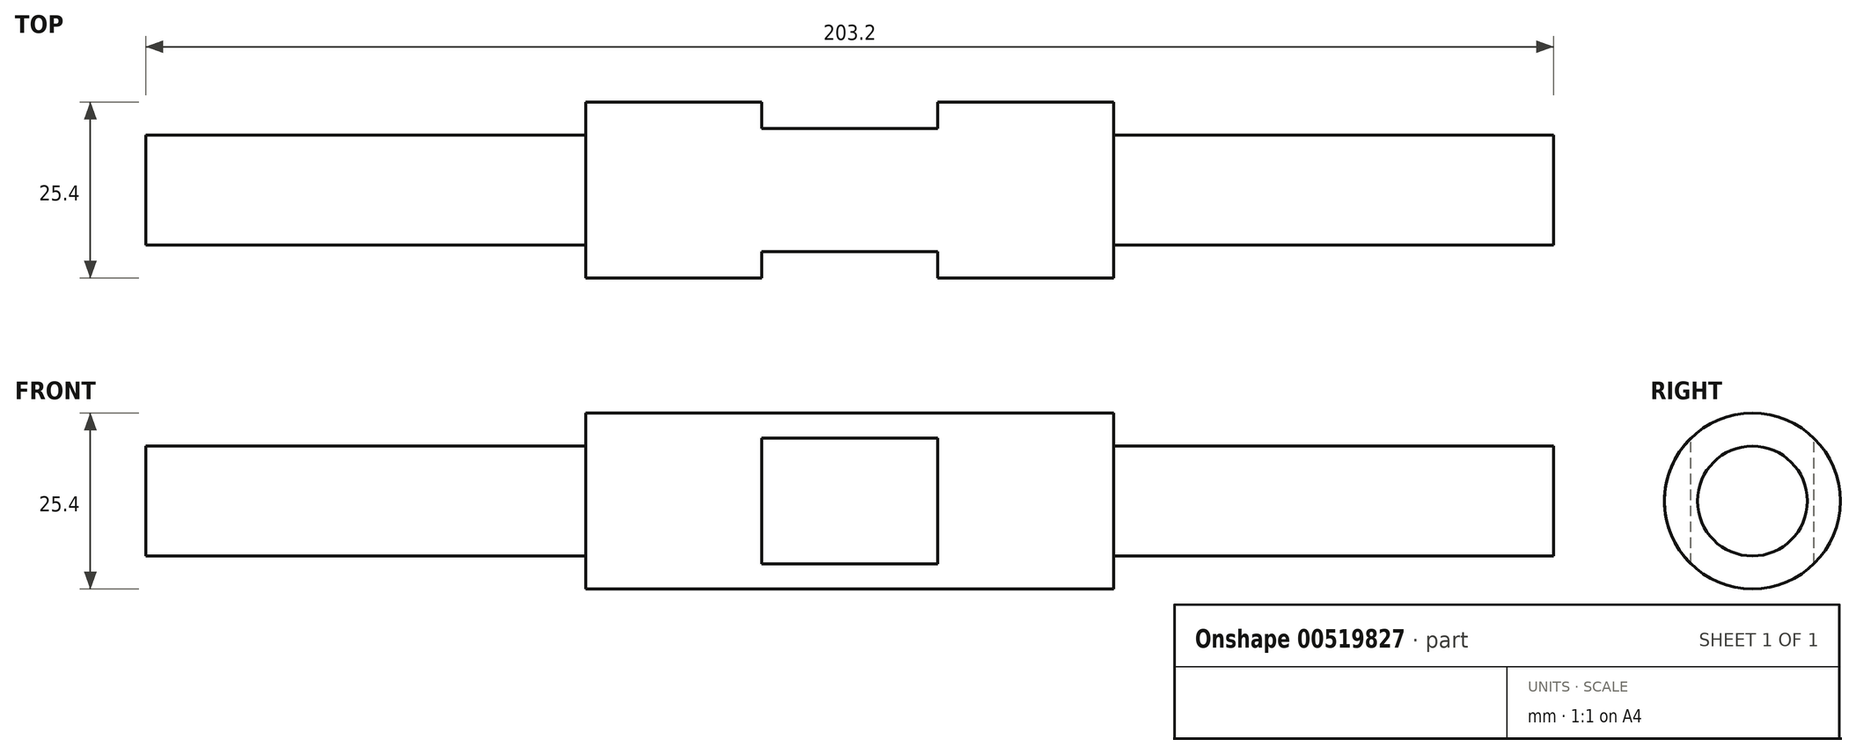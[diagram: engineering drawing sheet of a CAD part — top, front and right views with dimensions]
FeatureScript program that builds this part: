
annotation { "Feature Type Name" : "Feature", "Feature Type Description" : "" }
export const myFeature = defineFeature(function(context is Context, id is Id, definition is map)
    precondition{}
    {
        {
            var Q0;
            Q0=qCreatedBy(makeId("Front.planeOp"),FACE);
            var sketch = newSketch(context, id + "F0", { "sketchPlane" : qUnion([Q0])});
            skLineSegment(sketch, "E0", {"start": v(-173.84, 0) * mm, "end": v(181.18, 0) * mm, "construction": true});
            skLineSegment(sketch, "E1", {"start": v(-101.6, 0) * mm, "end": v(-101.6, 7.94) * mm});
            skLineSegment(sketch, "E2", {"start": v(-101.6, 7.94) * mm, "end": v(-38.1, 7.94) * mm});
            skLineSegment(sketch, "E3", {"start": v(-38.1, 7.94) * mm, "end": v(-38.1, 12.7) * mm});
            skLineSegment(sketch, "E4", {"start": v(-38.1, 12.7) * mm, "end": v(38.1, 12.7) * mm});
            skLineSegment(sketch, "E5", {"start": v(38.1, 12.7) * mm, "end": v(38.1, 7.94) * mm});
            skLineSegment(sketch, "E6", {"start": v(38.1, 7.94) * mm, "end": v(101.6, 7.94) * mm});
            skLineSegment(sketch, "E7", {"start": v(101.6, 7.94) * mm, "end": v(101.6, 0) * mm});
            skLineSegment(sketch, "E8", {"start": v(101.6, 0) * mm, "end": v(-101.6, 0) * mm});
            skSolve(sketch);
        }
        {
            var Q0;
            Q0 = qSketchRegion(id + "F0", true);
            var Q1;
            Q1=sQuery(id+"F0.wireOp",EDGE,"E8");
            revolve(context, id + "F1", {"entities" : qUnion([Q0]), "axis" : qUnion([Q1]), "revolveType" : RevolveType.FULL});
        }
        {
            var Q0;
            Q0=qCreatedBy(makeId("Top.planeOp"),FACE);
            cPlane(context, id + "F2", {"entities" : qUnion([Q0]), "cplaneType" : CPlaneType.OFFSET, "offset" : 12.7 * mm, "width" : 152.4 * mm, "height" : 152.4 * mm});
        }
        {
            var Q0;
            Q0=qCreatedBy(id+"F2.planeOp",FACE);
            var sketch = newSketch(context, id + "F3", { "sketchPlane" : qUnion([Q0])});
            skLineSegment(sketch, "E9", {"start": v(-46, 0) * mm, "end": v(65.9, 0) * mm, "construction": true});
            skLineSegment(sketch, "E10.bottom", {"start": v(12.7, 8.9) * mm, "end": v(-12.7, 8.89) * mm});
            skLineSegment(sketch, "E10.top", {"start": v(12.7, 16.51) * mm, "end": v(-12.7, 16.51) * mm});
            skLineSegment(sketch, "E10.left", {"start": v(12.7, 8.9) * mm, "end": v(12.7, 16.51) * mm});
            skLineSegment(sketch, "E10.right", {"start": v(-12.7, 8.89) * mm, "end": v(-12.7, 16.51) * mm});
            skPoint(sketch, "E10.middle", {"position": v(0, 12.7) * mm});
            skPoint(sketch, "E11.MirrorP", {"position": v(0, -12.7) * mm});
            skLineSegment(sketch, "E12.MirrorCS", {"start": v(12.7, -8.9) * mm, "end": v(12.7, -16.51) * mm});
            skLineSegment(sketch, "E13.MirrorCS", {"start": v(-12.7, -8.89) * mm, "end": v(-12.7, -16.51) * mm});
            skLineSegment(sketch, "E14.MirrorCS", {"start": v(12.7, -8.9) * mm, "end": v(-12.7, -8.89) * mm});
            skLineSegment(sketch, "E15.MirrorCS", {"start": v(12.7, -16.51) * mm, "end": v(-12.7, -16.51) * mm});
            skSolve(sketch);
        }
        {
            var Q0;
            Q0 = qSketchRegion(id + "F3", true);
            extrude(context, id + "F4", {"entities" : qUnion([Q0]), "operationType" : NewBodyOperationType.REMOVE, "oppositeDirection" : true, "depth" : 25.4 * mm, "offsetDistance" : 25.4 * mm});
        }
    });
